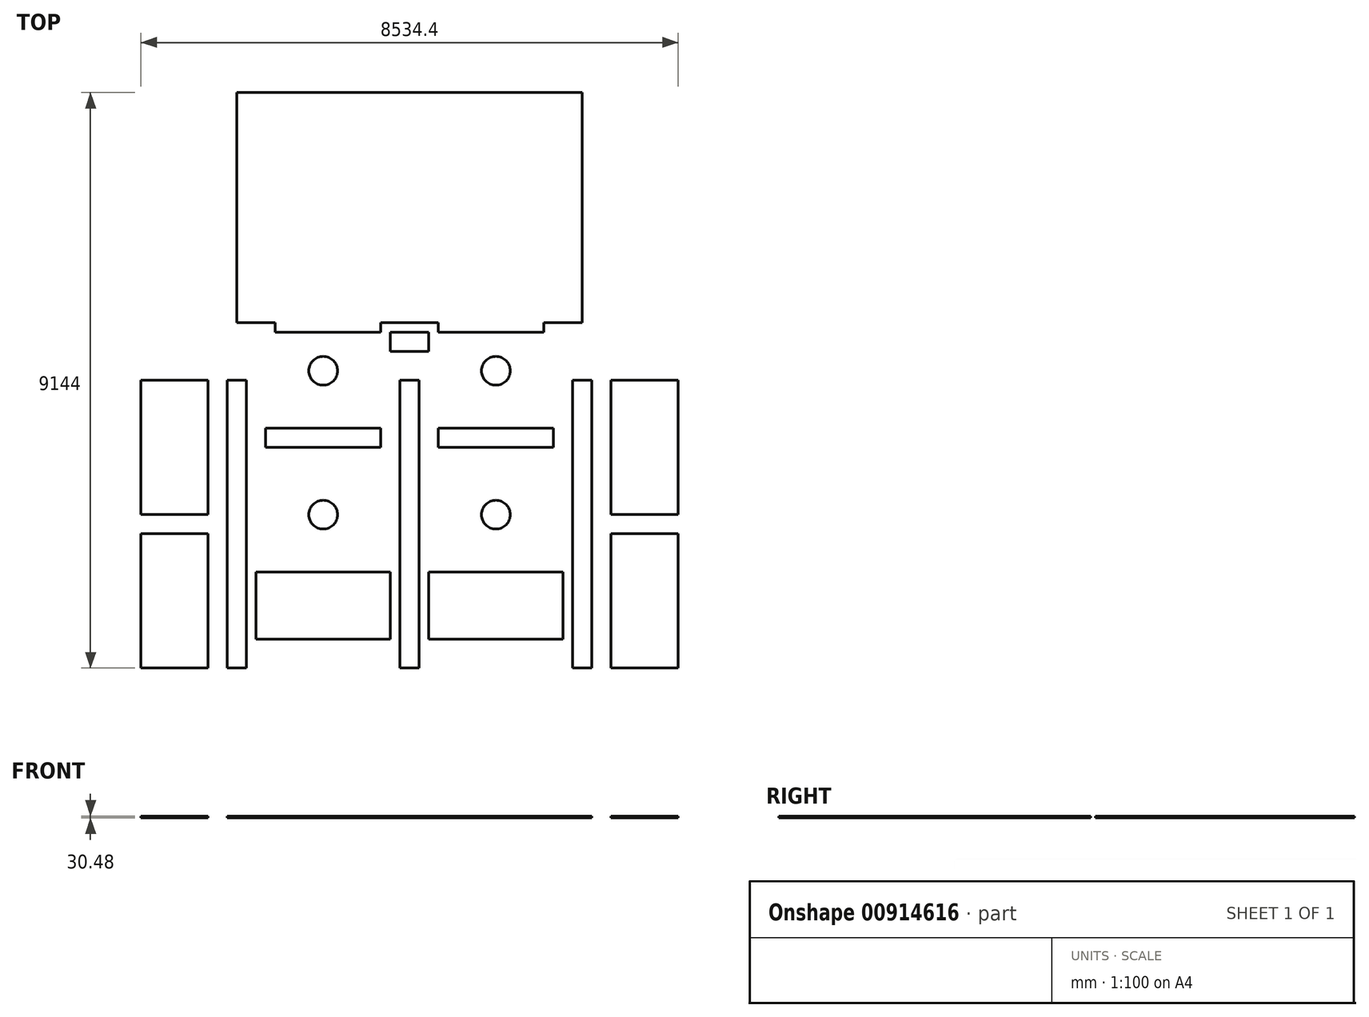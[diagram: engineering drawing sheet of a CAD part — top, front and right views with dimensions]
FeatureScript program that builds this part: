
annotation { "Feature Type Name" : "Feature", "Feature Type Description" : "" }
export const myFeature = defineFeature(function(context is Context, id is Id, definition is map)
    precondition{}
    {
        {
            var Q0;
            Q0=qCreatedBy(makeId("Top.planeOp"),FACE);
            var sketch = newSketch(context, id + "F0", { "sketchPlane" : qUnion([Q0])});
            skLineSegment(sketch, "E0.bottom", {"start": v(2743.2, 1828.8) * mm, "end": v(-2743.2, 1828.8) * mm});
            skLineSegment(sketch, "E0.top", {"start": v(2743.2, -1828.8) * mm, "end": v(-2743.2, -1828.8) * mm});
            skLineSegment(sketch, "E0.left", {"start": v(2743.2, 1828.8) * mm, "end": v(2743.2, -1828.8) * mm});
            skLineSegment(sketch, "E0.right", {"start": v(-2743.2, 1828.8) * mm, "end": v(-2743.2, -1828.8) * mm});
            skPoint(sketch, "E0.middle", {"position": v(0, 0) * mm});
            skSolve(sketch);
        }
        {
            var Q0;
            Q0=makeQuery(id+"F0.imprint","IMPRINT",FACE,{"disambiguationData":[TD([[makeQuery(id+"F0.imprint","IMPRINT",EDGE,{"derivedFrom":sQuery(id+"F0.wireOp",EDGE,"E0.bottom")}),1.0]])]});
            extrude(context, id + "F1", {"entities" : qUnion([Q0]), "depth" : 30.48 * mm, "offsetDistance" : 30.48 * mm});
        }
        {
            var Q0;
            Q0=qCreatedBy(makeId("Top.planeOp"),FACE);
            var sketch = newSketch(context, id + "F2", { "sketchPlane" : qUnion([Q0])});
            skLineSegment(sketch, "E1", {"start": v(0, 0) * mm, "end": v(0, -2743.2) * mm, "construction": true});
            skLineSegment(sketch, "E2", {"start": v(0, -2743.2) * mm, "end": v(152.4, -2743.2) * mm});
            skLineSegment(sketch, "E3", {"start": v(152.4, -2743.2) * mm, "end": v(152.4, -7315.2) * mm});
            skLineSegment(sketch, "E4", {"start": v(152.4, -7315.2) * mm, "end": v(-152.4, -7315.2) * mm});
            skLineSegment(sketch, "E5", {"start": v(-152.4, -7315.2) * mm, "end": v(-152.4, -2743.2) * mm});
            skLineSegment(sketch, "E6", {"start": v(-152.4, -2743.2) * mm, "end": v(0, -2743.2) * mm});
            skLineSegment(sketch, "E7", {"start": v(152.4, -2743.2) * mm, "end": v(2743.2, -2743.2) * mm, "construction": true});
            skLineSegment(sketch, "E8", {"start": v(2743.2, -2743.2) * mm, "end": v(2895.6, -2743.2) * mm});
            skLineSegment(sketch, "E9", {"start": v(2895.6, -2743.2) * mm, "end": v(2895.6, -7315.2) * mm});
            skLineSegment(sketch, "E10", {"start": v(2895.6, -7315.2) * mm, "end": v(2590.8, -7315.2) * mm});
            skLineSegment(sketch, "E11", {"start": v(2590.8, -7315.2) * mm, "end": v(2590.8, -2743.2) * mm});
            skLineSegment(sketch, "E12", {"start": v(2590.8, -2743.2) * mm, "end": v(2743.2, -2743.2) * mm});
            skLineSegment(sketch, "E13", {"start": v(0, -2743.2) * mm, "end": v(-2743.2, -2743.2) * mm, "construction": true});
            skLineSegment(sketch, "E14", {"start": v(-2743.2, -2743.2) * mm, "end": v(-2895.6, -2743.2) * mm});
            skLineSegment(sketch, "E15", {"start": v(-2895.6, -2743.2) * mm, "end": v(-2895.6, -7315.2) * mm});
            skLineSegment(sketch, "E16", {"start": v(-2895.6, -7315.2) * mm, "end": v(-2590.8, -7315.2) * mm});
            skLineSegment(sketch, "E17", {"start": v(-2590.8, -7315.2) * mm, "end": v(-2590.8, -2743.2) * mm});
            skLineSegment(sketch, "E18", {"start": v(-2590.8, -2743.2) * mm, "end": v(-2743.2, -2743.2) * mm});
            skSolve(sketch);
        }
        {
            var Q0;
            Q0 = qSketchRegion(id + "F2", true);
            extrude(context, id + "F3", {"entities" : qUnion([Q0]), "depth" : 30.48 * mm, "offsetDistance" : 30.48 * mm});
        }
        {
            var Q0;
            Q0=qCreatedBy(makeId("Top.planeOp"),FACE);
            var sketch = newSketch(context, id + "F4", { "sketchPlane" : qUnion([Q0])});
            skLineSegment(sketch, "E19", {"start": v(0, 0) * mm, "end": v(0, -7315.2) * mm, "construction": true});
            skLineSegment(sketch, "E20", {"start": v(0, -7315.2) * mm, "end": v(-3200.4, -7315.2) * mm, "construction": true});
            skLineSegment(sketch, "E21", {"start": v(-3200.4, -7315.2) * mm, "end": v(-3200.4, -5181.6) * mm});
            skLineSegment(sketch, "E22", {"start": v(-3200.4, -5181.6) * mm, "end": v(-4267.2, -5181.6) * mm});
            skLineSegment(sketch, "E23", {"start": v(-4267.2, -5181.6) * mm, "end": v(-4267.2, -7315.2) * mm});
            skLineSegment(sketch, "E24", {"start": v(-4267.2, -7315.2) * mm, "end": v(-3200.4, -7315.2) * mm});
            skLineSegment(sketch, "E25", {"start": v(-3200.4, -2743.2) * mm, "end": v(-4267.2, -2743.2) * mm});
            skLineSegment(sketch, "E26", {"start": v(-4267.2, -2743.2) * mm, "end": v(-4267.2, -4876.8) * mm});
            skLineSegment(sketch, "E27", {"start": v(-4267.2, -4876.8) * mm, "end": v(-3200.4, -4876.8) * mm});
            skLineSegment(sketch, "E28", {"start": v(-3200.4, -4876.8) * mm, "end": v(-3200.4, -2743.2) * mm});
            skLineSegment(sketch, "E29", {"start": v(-3200.4, -5181.6) * mm, "end": v(-3200.4, -4876.8) * mm, "construction": true});
            skLineSegment(sketch, "E30.MirrorCS", {"start": v(3200.4, -2743.2) * mm, "end": v(4267.2, -2743.2) * mm});
            skLineSegment(sketch, "E31.MirrorCS", {"start": v(3200.4, -4876.8) * mm, "end": v(3200.4, -2743.2) * mm});
            skLineSegment(sketch, "E32.MirrorCS", {"start": v(4267.2, -2743.2) * mm, "end": v(4267.2, -4876.8) * mm});
            skLineSegment(sketch, "E33.MirrorCS", {"start": v(4267.2, -4876.8) * mm, "end": v(3200.4, -4876.8) * mm});
            skLineSegment(sketch, "E34.MirrorCS", {"start": v(3200.4, -5181.6) * mm, "end": v(4267.2, -5181.6) * mm});
            skLineSegment(sketch, "E35.MirrorCS", {"start": v(3200.4, -7315.2) * mm, "end": v(3200.4, -5181.6) * mm});
            skLineSegment(sketch, "E36.MirrorCS", {"start": v(4267.2, -5181.6) * mm, "end": v(4267.2, -7315.2) * mm});
            skLineSegment(sketch, "E37.MirrorCS", {"start": v(4267.2, -7315.2) * mm, "end": v(3200.4, -7315.2) * mm});
            skSolve(sketch);
        }
        {
            var Q0;
            Q0 = qSketchRegion(id + "F4", true);
            extrude(context, id + "F5", {"entities" : qUnion([Q0]), "depth" : 30.48 * mm, "offsetDistance" : 30.48 * mm});
        }
        {
            var Q0;
            Q0=qCreatedBy(makeId("Top.planeOp"),FACE);
            var sketch = newSketch(context, id + "F6", { "sketchPlane" : qUnion([Q0])});
            skLineSegment(sketch, "E38", {"start": v(0, 0) * mm, "end": v(0, -1981.2) * mm, "construction": true});
            skLineSegment(sketch, "E39", {"start": v(0, -1981.2) * mm, "end": v(-304.8, -1981.2) * mm});
            skLineSegment(sketch, "E40", {"start": v(-304.8, -1981.2) * mm, "end": v(-304.8, -2286) * mm});
            skLineSegment(sketch, "E41", {"start": v(-304.8, -2286) * mm, "end": v(304.8, -2286) * mm});
            skLineSegment(sketch, "E42", {"start": v(304.8, -2286) * mm, "end": v(304.8, -1981.2) * mm});
            skLineSegment(sketch, "E43", {"start": v(304.8, -1981.2) * mm, "end": v(0, -1981.2) * mm});
            skSolve(sketch);
        }
        {
            var Q0;
            Q0 = qSketchRegion(id + "F6", true);
            extrude(context, id + "F7", {"entities" : qUnion([Q0]), "depth" : 30.48 * mm, "offsetDistance" : 30.48 * mm});
        }
        {
            var Q0;
            Q0=qCreatedBy(makeId("Top.planeOp"),FACE);
            var sketch = newSketch(context, id + "F8", { "sketchPlane" : qUnion([Q0])});
            skLineSegment(sketch, "E44", {"start": v(0, 0) * mm, "end": v(0, -1828.8) * mm, "construction": true});
            skLineSegment(sketch, "E45", {"start": v(0, -1828.8) * mm, "end": v(457.2, -1828.8) * mm, "construction": true});
            skLineSegment(sketch, "E46", {"start": v(457.2, -1828.8) * mm, "end": v(457.2, -1981.2) * mm});
            skLineSegment(sketch, "E47", {"start": v(457.2, -1981.2) * mm, "end": v(2133.6, -1981.2) * mm});
            skLineSegment(sketch, "E48", {"start": v(2133.6, -1981.2) * mm, "end": v(2133.6, -1828.8) * mm});
            skLineSegment(sketch, "E49", {"start": v(2133.6, -1828.8) * mm, "end": v(457.2, -1828.8) * mm});
            skLineSegment(sketch, "E50.MirrorCS", {"start": v(-457.2, -1981.2) * mm, "end": v(-2133.6, -1981.2) * mm});
            skLineSegment(sketch, "E51.MirrorCS", {"start": v(-2133.6, -1981.2) * mm, "end": v(-2133.6, -1828.8) * mm});
            skLineSegment(sketch, "E52.MirrorCS", {"start": v(-2133.6, -1828.8) * mm, "end": v(-457.2, -1828.8) * mm});
            skLineSegment(sketch, "E53.MirrorCS", {"start": v(-457.2, -1828.8) * mm, "end": v(-457.2, -1981.2) * mm});
            skSolve(sketch);
        }
        {
            var Q0;
            Q0 = qSketchRegion(id + "F8", true);
            extrude(context, id + "F9", {"entities" : qUnion([Q0]), "operationType" : NewBodyOperationType.ADD, "depth" : 30.48 * mm, "offsetDistance" : 30.48 * mm});
        }
        {
            var Q0;
            Q0=qCreatedBy(makeId("Top.planeOp"),FACE);
            var sketch = newSketch(context, id + "F10", { "sketchPlane" : qUnion([Q0])});
            skLineSegment(sketch, "E54", {"start": v(0, 0) * mm, "end": v(0, -3657.6) * mm, "construction": true});
            skLineSegment(sketch, "E55", {"start": v(0, -3657.6) * mm, "end": v(457.2, -3657.6) * mm, "construction": true});
            skLineSegment(sketch, "E56", {"start": v(457.2, -3657.6) * mm, "end": v(457.2, -3810) * mm});
            skLineSegment(sketch, "E57", {"start": v(457.2, -3810) * mm, "end": v(2286, -3810) * mm});
            skLineSegment(sketch, "E58", {"start": v(2286, -3810) * mm, "end": v(2286, -3505.2) * mm});
            skLineSegment(sketch, "E59", {"start": v(2286, -3505.2) * mm, "end": v(457.2, -3505.2) * mm});
            skLineSegment(sketch, "E60", {"start": v(457.2, -3505.2) * mm, "end": v(457.2, -3657.6) * mm});
            skLineSegment(sketch, "E61.MirrorCS", {"start": v(-457.2, -3657.6) * mm, "end": v(-457.2, -3810) * mm});
            skLineSegment(sketch, "E62.MirrorCS", {"start": v(-457.2, -3810) * mm, "end": v(-2286, -3810) * mm});
            skLineSegment(sketch, "E63.MirrorCS", {"start": v(-457.2, -3505.2) * mm, "end": v(-457.2, -3657.6) * mm});
            skLineSegment(sketch, "E64.MirrorCS", {"start": v(-2286, -3505.2) * mm, "end": v(-457.2, -3505.2) * mm});
            skLineSegment(sketch, "E65.MirrorCS", {"start": v(-2286, -3810) * mm, "end": v(-2286, -3505.2) * mm});
            skSolve(sketch);
        }
        {
            var Q0;
            Q0 = qSketchRegion(id + "F10", true);
            extrude(context, id + "F11", {"entities" : qUnion([Q0]), "depth" : 30.48 * mm, "offsetDistance" : 30.48 * mm});
        }
        {
            var Q0;
            Q0=qCreatedBy(makeId("Top.planeOp"),FACE);
            var sketch = newSketch(context, id + "F12", { "sketchPlane" : qUnion([Q0])});
            skLineSegment(sketch, "E66", {"start": v(0, 0) * mm, "end": v(0, -5791.2) * mm, "construction": true});
            skLineSegment(sketch, "E67", {"start": v(0, -5791.2) * mm, "end": v(-304.8, -5791.2) * mm, "construction": true});
            skLineSegment(sketch, "E68", {"start": v(-304.8, -5791.2) * mm, "end": v(-2438.4, -5791.2) * mm});
            skLineSegment(sketch, "E69", {"start": v(-2438.4, -5791.2) * mm, "end": v(-2438.4, -6858) * mm});
            skLineSegment(sketch, "E70", {"start": v(-2438.4, -6858) * mm, "end": v(-304.8, -6858) * mm});
            skLineSegment(sketch, "E71", {"start": v(-304.8, -6858) * mm, "end": v(-304.8, -5791.2) * mm});
            skLineSegment(sketch, "E72.MirrorCS", {"start": v(304.8, -5791.2) * mm, "end": v(2438.4, -5791.2) * mm});
            skLineSegment(sketch, "E73.MirrorCS", {"start": v(304.8, -6858) * mm, "end": v(304.8, -5791.2) * mm});
            skLineSegment(sketch, "E74.MirrorCS", {"start": v(2438.4, -6858) * mm, "end": v(304.8, -6858) * mm});
            skLineSegment(sketch, "E75.MirrorCS", {"start": v(2438.4, -5791.2) * mm, "end": v(2438.4, -6858) * mm});
            skSolve(sketch);
        }
        {
            var Q0;
            Q0 = qSketchRegion(id + "F12", true);
            extrude(context, id + "F13", {"entities" : qUnion([Q0]), "depth" : 30.48 * mm, "offsetDistance" : 30.48 * mm});
        }
        {
            var Q0;
            Q0=qCreatedBy(makeId("Top.planeOp"),FACE);
            var sketch = newSketch(context, id + "F14", { "sketchPlane" : qUnion([Q0])});
            skLineSegment(sketch, "E76", {"start": v(0, 0) * mm, "end": v(0, -2590.8) * mm, "construction": true});
            skLineSegment(sketch, "E77", {"start": v(0, -2590.8) * mm, "end": v(-1371.6, -2590.8) * mm, "construction": true});
            skLineSegment(sketch, "E78", {"start": v(0, -2590.8) * mm, "end": v(1371.6, -2590.8) * mm, "construction": true});
            skLineSegment(sketch, "E79", {"start": v(1371.6, -2590.8) * mm, "end": v(1371.6, -4876.8) * mm, "construction": true});
            skLineSegment(sketch, "E80", {"start": v(-1371.6, -2590.8) * mm, "end": v(-1371.6, -4876.8) * mm, "construction": true});
            skCircle(sketch, "E81", {"center": v(-1371.6, -2590.8) * mm, "radius": 228.6 * mm});
            skCircle(sketch, "E82", {"center": v(1371.6, -2590.8) * mm, "radius": 228.6 * mm});
            skCircle(sketch, "E83", {"center": v(1371.6, -4876.8) * mm, "radius": 228.6 * mm});
            skCircle(sketch, "E84", {"center": v(-1371.6, -4876.8) * mm, "radius": 228.6 * mm});
            skSolve(sketch);
        }
        {
            var Q0;
            Q0 = qSketchRegion(id + "F14", true);
            extrude(context, id + "F15", {"entities" : qUnion([Q0]), "depth" : 30.48 * mm, "offsetDistance" : 30.48 * mm});
        }
    });
